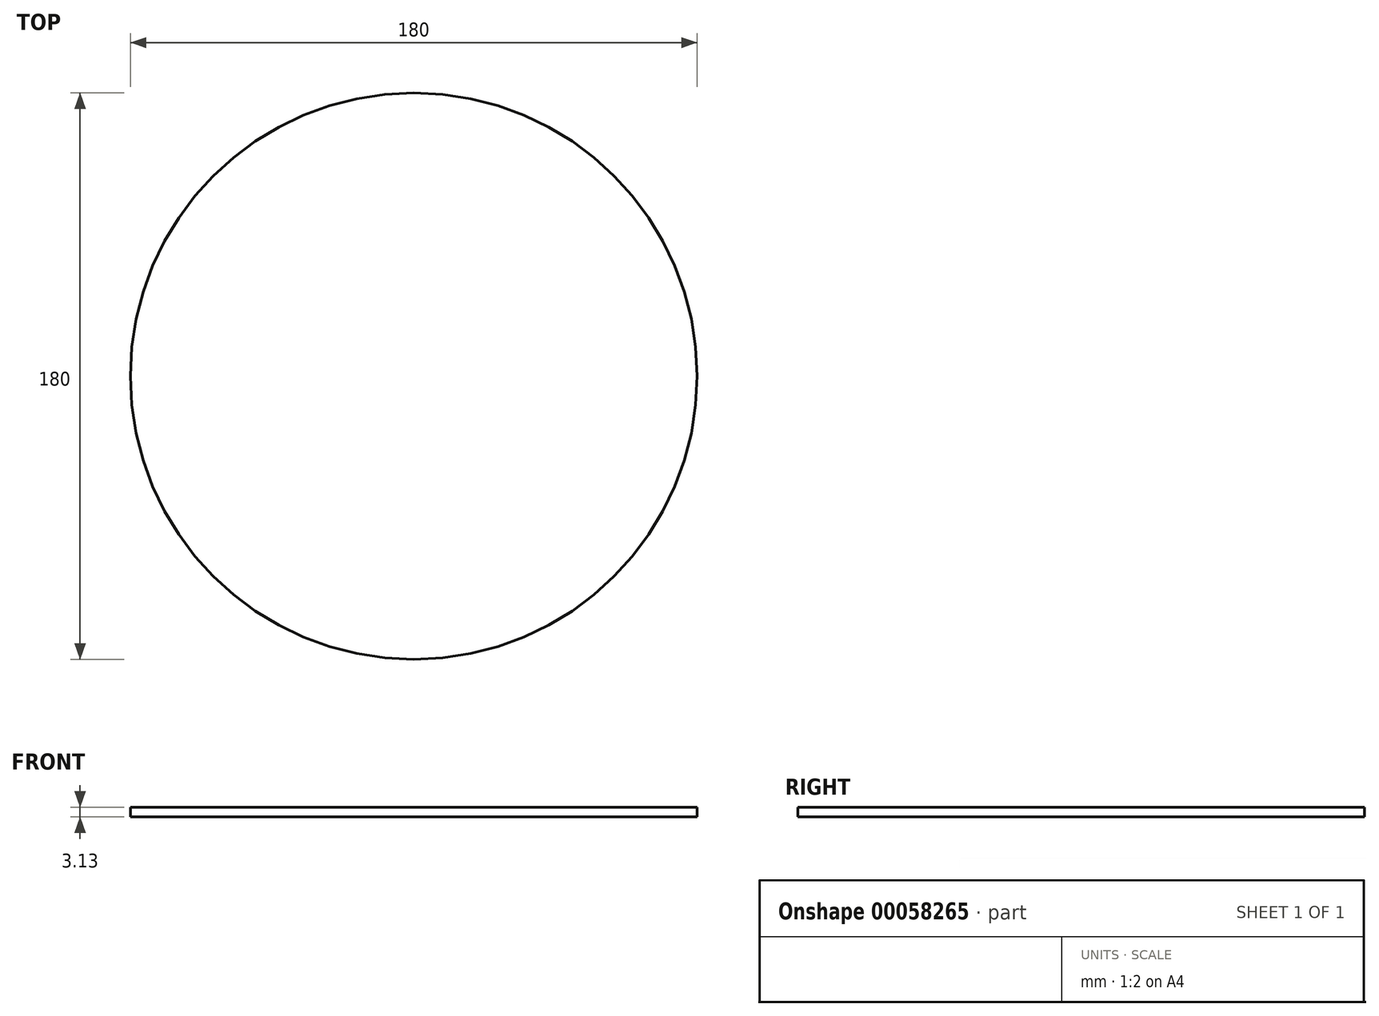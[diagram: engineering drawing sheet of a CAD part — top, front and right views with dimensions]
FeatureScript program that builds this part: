
annotation { "Feature Type Name" : "Feature", "Feature Type Description" : "" }
export const myFeature = defineFeature(function(context is Context, id is Id, definition is map)
    precondition{}
    {
        {
            var Q0;
            Q0=qCreatedBy(makeId("Top.planeOp"),FACE);
            var sketch = newSketch(context, id + "F0", { "sketchPlane" : qUnion([Q0])});
            skCircle(sketch, "E0", {"center": v(0, 0) * mm, "radius": 90 * mm});
            skSolve(sketch);
        }
        {
            var Q0;
            Q0 = qSketchRegion(id + "F0", true);
            extrude(context, id + "F1", {"entities" : qUnion([Q0]), "depth" : 3.12 * mm});
        }
    });
